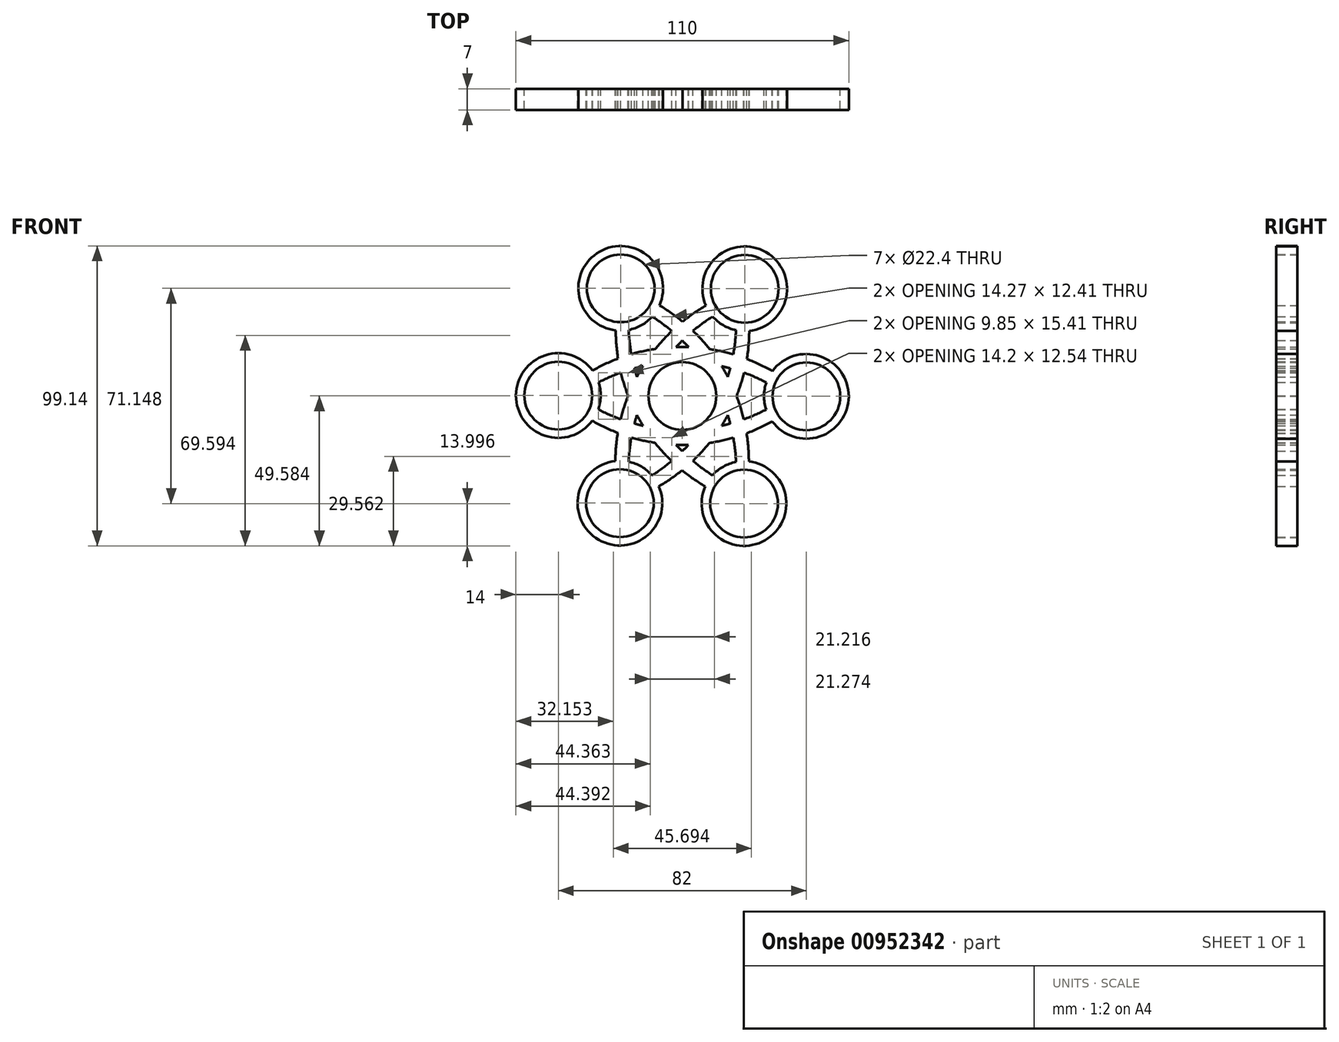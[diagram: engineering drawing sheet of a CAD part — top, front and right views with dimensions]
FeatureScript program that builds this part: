
annotation { "Feature Type Name" : "Feature", "Feature Type Description" : "" }
export const myFeature = defineFeature(function(context is Context, id is Id, definition is map)
    precondition{}
    {
        {
            var Q0;
            Q0=qCreatedBy(makeId("Front.planeOp"),FACE);
            var sketch = newSketch(context, id + "F0", { "sketchPlane" : qUnion([Q0])});
            skCircle(sketch, "E0", {"center": v(0, 0) * mm, "radius": 11.2 * mm});
            skCircle(sketch, "E1.cCircle", {"center": v(0, 0) * mm, "radius": 35.5 * mm, "construction": true});
            skLineSegment(sketch, "E1.0", {"start": v(20.62, 35.44) * mm, "end": v(41, -0.13) * mm});
            skLineSegment(sketch, "E1.1", {"start": v(41, -0.13) * mm, "end": v(20.38, -35.57) * mm});
            skLineSegment(sketch, "E1.2", {"start": v(20.38, -35.57) * mm, "end": v(-20.62, -35.44) * mm});
            skLineSegment(sketch, "E1.3", {"start": v(-20.62, -35.44) * mm, "end": v(-41, 0.13) * mm});
            skLineSegment(sketch, "E1.4", {"start": v(-41, 0.13) * mm, "end": v(-20.38, 35.57) * mm});
            skLineSegment(sketch, "E1.5", {"start": v(-20.38, 35.57) * mm, "end": v(20.62, 35.44) * mm});
            skPoint(sketch, "E1.0.midPoint", {"position": v(30.8, 17.65) * mm});
            skArc(sketch, "E2", {"start": v(-20.62, -35.44) * mm, "mid": v(14, -8.14) * mm, "end": v(20.62, 35.44) * mm});
            skArc(sketch, "E3", {"start": v(20.62, 35.44) * mm, "mid": v(-14, 8.14) * mm, "end": v(-20.62, -35.44) * mm});
            skArc(sketch, "E4", {"start": v(20.38, -35.57) * mm, "mid": v(14.05, 8.05) * mm, "end": v(-20.38, 35.57) * mm});
            skArc(sketch, "E5", {"start": v(-20.38, 35.57) * mm, "mid": v(-14.05, -8.05) * mm, "end": v(20.38, -35.57) * mm});
            skArc(sketch, "E6", {"start": v(41, -0.13) * mm, "mid": v(0.05, 16.2) * mm, "end": v(-41, 0.13) * mm});
            skArc(sketch, "E7", {"start": v(-41, 0.13) * mm, "mid": v(-0.05, -16.2) * mm, "end": v(41, -0.13) * mm});
            skCircle(sketch, "E8.cCircle", {"center": v(0, 0) * mm, "radius": 30.31 * mm, "construction": true});
            skLineSegment(sketch, "E8.0", {"start": v(17.5, -30.31) * mm, "end": v(-17.5, -30.31) * mm});
            skLineSegment(sketch, "E8.1", {"start": v(-17.5, -30.31) * mm, "end": v(-35, 0) * mm});
            skLineSegment(sketch, "E8.2", {"start": v(-35, 0) * mm, "end": v(-17.5, 30.31) * mm});
            skLineSegment(sketch, "E8.3", {"start": v(-17.5, 30.31) * mm, "end": v(17.5, 30.31) * mm});
            skLineSegment(sketch, "E8.4", {"start": v(17.5, 30.31) * mm, "end": v(35, 0) * mm});
            skLineSegment(sketch, "E8.5", {"start": v(35, 0) * mm, "end": v(17.5, -30.31) * mm});
            skPoint(sketch, "E8.0.midPoint", {"position": v(0, -30.31) * mm});
            skArc(sketch, "E9", {"start": v(-17.5, -30.31) * mm, "mid": v(9.76, -5.63) * mm, "end": v(17.5, 30.31) * mm});
            skArc(sketch, "E10", {"start": v(17.5, 30.31) * mm, "mid": v(-9.76, 5.63) * mm, "end": v(-17.5, -30.31) * mm});
            skArc(sketch, "E11", {"start": v(17.5, -30.31) * mm, "mid": v(9.76, 5.63) * mm, "end": v(-17.5, 30.31) * mm});
            skArc(sketch, "E12", {"start": v(-17.5, 30.31) * mm, "mid": v(-9.76, -5.63) * mm, "end": v(17.5, -30.31) * mm});
            skArc(sketch, "E13", {"start": v(35, 0) * mm, "mid": v(0, 11.27) * mm, "end": v(-35, 0) * mm});
            skArc(sketch, "E14", {"start": v(-35, 0) * mm, "mid": v(0, -11.27) * mm, "end": v(35, 0) * mm});
            skCircle(sketch, "E15", {"center": v(20.62, 35.44) * mm, "radius": 14 * mm});
            skCircle(sketch, "E16", {"center": v(-20.38, 35.57) * mm, "radius": 14 * mm});
            skCircle(sketch, "E17", {"center": v(-41, 0.13) * mm, "radius": 14 * mm});
            skCircle(sketch, "E18", {"center": v(-20.62, -35.44) * mm, "radius": 14 * mm});
            skCircle(sketch, "E19", {"center": v(20.38, -35.57) * mm, "radius": 14 * mm});
            skCircle(sketch, "E20", {"center": v(41, -0.13) * mm, "radius": 14 * mm});
            skCircle(sketch, "E21", {"center": v(20.62, 35.44) * mm, "radius": 11.2 * mm});
            skCircle(sketch, "E22", {"center": v(41, -0.13) * mm, "radius": 11.2 * mm});
            skCircle(sketch, "E23", {"center": v(20.38, -35.57) * mm, "radius": 11.2 * mm});
            skCircle(sketch, "E24", {"center": v(-20.62, -35.44) * mm, "radius": 11.2 * mm});
            skCircle(sketch, "E25", {"center": v(-41, 0.13) * mm, "radius": 11.2 * mm});
            skCircle(sketch, "E26", {"center": v(-20.38, 35.57) * mm, "radius": 11.2 * mm});
            skSolve(sketch);
        }
        {
            var Q0;
            {var subQ0=sQuery(id+"F0.wireOp",EDGE,"E16");var subQ1=sQuery(id+"F0.wireOp",EDGE,"E1.4");var subQ2=makeQuery(id+"F0.imprint","INTERSECT",VERTEX,{"derivedFrom":[subQ1,subQ0]});Q0=makeQuery(id+"F0.imprint","IMPRINT",FACE,{"disambiguationData":[TD([[makeQuery(id+"F0.imprint","IMPRINT",EDGE,{"disambiguationData":[TD([[subQ2,-1.0]])],"derivedFrom":subQ1}),1.0]])]});}
            var Q1;
            {var subQ0=sQuery(id+"F0.wireOp",EDGE,"E16");var subQ1=sQuery(id+"F0.wireOp",EDGE,"E1.5");var subQ2=makeQuery(id+"F0.imprint","INTERSECT",VERTEX,{"derivedFrom":[subQ1,subQ0]});Q1=makeQuery(id+"F0.imprint","IMPRINT",FACE,{"disambiguationData":[TD([[makeQuery(id+"F0.imprint","IMPRINT",EDGE,{"disambiguationData":[TD([[subQ2,1.0]])],"derivedFrom":subQ1}),-1.0]])]});}
            var Q2;
            {var subQ0=sQuery(id+"F0.wireOp",EDGE,"E16");var subQ5=sQuery(id+"F0.wireOp",EDGE,"E4");var subQ6=makeQuery(id+"F0.imprint","INTERSECT",VERTEX,{"derivedFrom":[subQ5,subQ0]});Q2=makeQuery(id+"F0.imprint","IMPRINT",FACE,{"disambiguationData":[TD([[makeQuery(id+"F0.imprint","IMPRINT",EDGE,{"disambiguationData":[TD([[subQ6,-1.0]])],"derivedFrom":subQ5}),1.0]])]});}
            var Q3;
            {var subQ0=sQuery(id+"F0.wireOp",EDGE,"E8.3");var subQ1=sQuery(id+"F0.wireOp",EDGE,"E4");var subQ2=makeQuery(id+"F0.imprint","INTERSECT",VERTEX,{"derivedFrom":[subQ1,subQ0]});Q3=makeQuery(id+"F0.imprint","IMPRINT",FACE,{"disambiguationData":[TD([[makeQuery(id+"F0.imprint","IMPRINT",EDGE,{"disambiguationData":[TD([[subQ2,-1.0]])],"derivedFrom":subQ1}),1.0]])]});}
            var Q4;
            {var subQ0=sQuery(id+"F0.wireOp",EDGE,"E16");var subQ1=sQuery(id+"F0.wireOp",EDGE,"E11");var subQ2=makeQuery(id+"F0.imprint","INTERSECT",VERTEX,{"derivedFrom":[subQ1,subQ0]});Q4=makeQuery(id+"F0.imprint","IMPRINT",FACE,{"disambiguationData":[TD([[makeQuery(id+"F0.imprint","IMPRINT",EDGE,{"disambiguationData":[TD([[subQ2,-1.0]])],"derivedFrom":subQ1}),1.0]])]});}
            var Q5;
            {var subQ1=sQuery(id+"F0.wireOp",EDGE,"E5");var subQ5=sQuery(id+"F0.wireOp",EDGE,"E8.2");var subQ6=makeQuery(id+"F0.imprint","INTERSECT",VERTEX,{"derivedFrom":[subQ1,subQ5]});Q5=makeQuery(id+"F0.imprint","IMPRINT",FACE,{"disambiguationData":[TD([[makeQuery(id+"F0.imprint","IMPRINT",EDGE,{"disambiguationData":[TD([[subQ6,-1.0]])],"derivedFrom":subQ1}),1.0]])]});}
            var Q6;
            {var subQ5=sQuery(id+"F0.wireOp",EDGE,"E16");var subQ6=sQuery(id+"F0.wireOp",EDGE,"E1.4");var subQ7=makeQuery(id+"F0.imprint","INTERSECT",VERTEX,{"derivedFrom":[subQ6,subQ5]});Q6=makeQuery(id+"F0.imprint","IMPRINT",FACE,{"disambiguationData":[TD([[makeQuery(id+"F0.imprint","IMPRINT",EDGE,{"disambiguationData":[TD([[subQ7,-1.0]])],"derivedFrom":subQ6}),-1.0]])]});}
            var Q7;
            {var subQ0=sQuery(id+"F0.wireOp",EDGE,"E8.2");var subQ1=sQuery(id+"F0.wireOp",EDGE,"E5");var subQ2=makeQuery(id+"F0.imprint","INTERSECT",VERTEX,{"derivedFrom":[subQ1,subQ0]});Q7=makeQuery(id+"F0.imprint","IMPRINT",FACE,{"disambiguationData":[TD([[makeQuery(id+"F0.imprint","IMPRINT",EDGE,{"disambiguationData":[TD([[subQ2,-1.0]])],"derivedFrom":subQ1}),-1.0]])]});}
            var Q8;
            {var subQ0=sQuery(id+"F0.wireOp",EDGE,"E26");var subQ1=sQuery(id+"F0.wireOp",EDGE,"E5");var subQ2=makeQuery(id+"F0.imprint","INTERSECT",VERTEX,{"derivedFrom":[subQ1,subQ0]});Q8=makeQuery(id+"F0.imprint","IMPRINT",FACE,{"disambiguationData":[TD([[makeQuery(id+"F0.imprint","IMPRINT",EDGE,{"disambiguationData":[TD([[subQ2,-1.0]])],"derivedFrom":subQ1}),1.0]])]});}
            var Q9;
            {var subQ0=sQuery(id+"F0.wireOp",EDGE,"E16");var subQ1=sQuery(id+"F0.wireOp",EDGE,"E4");var subQ2=makeQuery(id+"F0.imprint","INTERSECT",VERTEX,{"derivedFrom":[subQ1,subQ0]});Q9=makeQuery(id+"F0.imprint","IMPRINT",FACE,{"disambiguationData":[TD([[makeQuery(id+"F0.imprint","IMPRINT",EDGE,{"disambiguationData":[TD([[subQ2,-1.0]])],"derivedFrom":subQ1}),-1.0]])]});}
            var Q10;
            {var subQ0=sQuery(id+"F0.wireOp",EDGE,"E4");var subQ1=sQuery(id+"F0.wireOp",EDGE,"E3");var subQ2=makeQuery(id+"F0.imprint","INTERSECT",VERTEX,{"derivedFrom":[subQ1,subQ0]});Q10=makeQuery(id+"F0.imprint","IMPRINT",FACE,{"disambiguationData":[TD([[makeQuery(id+"F0.imprint","IMPRINT",EDGE,{"disambiguationData":[TD([[subQ2,-1.0]])],"derivedFrom":subQ1}),-1.0]])]});}
            var Q11;
            {var subQ0=sQuery(id+"F0.wireOp",EDGE,"E16");var subQ1=sQuery(id+"F0.wireOp",EDGE,"E5");var subQ2=makeQuery(id+"F0.imprint","INTERSECT",VERTEX,{"derivedFrom":[subQ1,subQ0]});Q11=makeQuery(id+"F0.imprint","IMPRINT",FACE,{"disambiguationData":[TD([[makeQuery(id+"F0.imprint","IMPRINT",EDGE,{"disambiguationData":[TD([[subQ2,-1.0]])],"derivedFrom":subQ1}),1.0]])]});}
            var Q12;
            {var subQ0=sQuery(id+"F0.wireOp",EDGE,"E6");var subQ1=sQuery(id+"F0.wireOp",EDGE,"E5");var subQ2=makeQuery(id+"F0.imprint","INTERSECT",VERTEX,{"derivedFrom":[subQ1,subQ0]});Q12=makeQuery(id+"F0.imprint","IMPRINT",FACE,{"disambiguationData":[TD([[makeQuery(id+"F0.imprint","IMPRINT",EDGE,{"disambiguationData":[TD([[subQ2,-1.0]])],"derivedFrom":subQ1}),1.0]])]});}
            var Q13;
            {var subQ0=sQuery(id+"F0.wireOp",EDGE,"E6");var subQ1=sQuery(id+"F0.wireOp",EDGE,"E3");var subQ2=makeQuery(id+"F0.imprint","INTERSECT",VERTEX,{"derivedFrom":[subQ1,subQ0]});Q13=makeQuery(id+"F0.imprint","IMPRINT",FACE,{"disambiguationData":[TD([[makeQuery(id+"F0.imprint","IMPRINT",EDGE,{"disambiguationData":[TD([[subQ2,-1.0]])],"derivedFrom":subQ1}),-1.0]])]});}
            var Q14;
            {var subQ0=sQuery(id+"F0.wireOp",EDGE,"E11");var subQ1=sQuery(id+"F0.wireOp",EDGE,"E3");var subQ2=makeQuery(id+"F0.imprint","INTERSECT",VERTEX,{"derivedFrom":[subQ1,subQ0]});Q14=makeQuery(id+"F0.imprint","IMPRINT",FACE,{"disambiguationData":[TD([[makeQuery(id+"F0.imprint","IMPRINT",EDGE,{"disambiguationData":[TD([[subQ2,-1.0]])],"derivedFrom":subQ1}),1.0]])]});}
            var Q15;
            {var subQ0=sQuery(id+"F0.wireOp",EDGE,"E4");var subQ1=sQuery(id+"F0.wireOp",EDGE,"E3");var subQ2=makeQuery(id+"F0.imprint","INTERSECT",VERTEX,{"derivedFrom":[subQ1,subQ0]});Q15=makeQuery(id+"F0.imprint","IMPRINT",FACE,{"disambiguationData":[TD([[makeQuery(id+"F0.imprint","IMPRINT",EDGE,{"disambiguationData":[TD([[subQ2,-1.0]])],"derivedFrom":subQ1}),1.0]])]});}
            var Q16;
            {var subQ0=sQuery(id+"F0.wireOp",EDGE,"E6");var subQ1=sQuery(id+"F0.wireOp",EDGE,"E3");var subQ2=makeQuery(id+"F0.imprint","INTERSECT",VERTEX,{"derivedFrom":[subQ1,subQ0]});Q16=makeQuery(id+"F0.imprint","IMPRINT",FACE,{"disambiguationData":[TD([[makeQuery(id+"F0.imprint","IMPRINT",EDGE,{"disambiguationData":[TD([[subQ2,-1.0]])],"derivedFrom":subQ1}),1.0]])]});}
            var Q17;
            {var subQ0=sQuery(id+"F0.wireOp",EDGE,"E11");var subQ1=sQuery(id+"F0.wireOp",EDGE,"E6");var subQ2=makeQuery(id+"F0.imprint","INTERSECT",VERTEX,{"derivedFrom":[subQ1,subQ0]});Q17=makeQuery(id+"F0.imprint","IMPRINT",FACE,{"disambiguationData":[TD([[makeQuery(id+"F0.imprint","IMPRINT",EDGE,{"disambiguationData":[TD([[subQ2,-1.0]])],"derivedFrom":subQ1}),1.0]])]});}
            var Q18;
            {var subQ0=sQuery(id+"F0.wireOp",EDGE,"E6");var subQ1=sQuery(id+"F0.wireOp",EDGE,"E4");var subQ2=makeQuery(id+"F0.imprint","INTERSECT",VERTEX,{"derivedFrom":[subQ1,subQ0]});Q18=makeQuery(id+"F0.imprint","IMPRINT",FACE,{"disambiguationData":[TD([[makeQuery(id+"F0.imprint","IMPRINT",EDGE,{"disambiguationData":[TD([[subQ2,-1.0]])],"derivedFrom":subQ1}),1.0]])]});}
            var Q19;
            {var subQ0=sQuery(id+"F0.wireOp",EDGE,"E13");var subQ1=sQuery(id+"F0.wireOp",EDGE,"E4");var subQ2=makeQuery(id+"F0.imprint","INTERSECT",VERTEX,{"derivedFrom":[subQ1,subQ0]});Q19=makeQuery(id+"F0.imprint","IMPRINT",FACE,{"disambiguationData":[TD([[makeQuery(id+"F0.imprint","IMPRINT",EDGE,{"disambiguationData":[TD([[subQ2,-1.0]])],"derivedFrom":subQ1}),1.0]])]});}
            var Q20;
            {var subQ0=sQuery(id+"F0.wireOp",EDGE,"E12");var subQ1=sQuery(id+"F0.wireOp",EDGE,"E3");var subQ2=makeQuery(id+"F0.imprint","INTERSECT",VERTEX,{"derivedFrom":[subQ1,subQ0]});Q20=makeQuery(id+"F0.imprint","IMPRINT",FACE,{"disambiguationData":[TD([[makeQuery(id+"F0.imprint","IMPRINT",EDGE,{"disambiguationData":[TD([[subQ2,-1.0]])],"derivedFrom":subQ1}),-1.0]])]});}
            var Q21;
            {var subQ0=sQuery(id+"F0.wireOp",EDGE,"E12");var subQ1=sQuery(id+"F0.wireOp",EDGE,"E3");var subQ2=makeQuery(id+"F0.imprint","INTERSECT",VERTEX,{"derivedFrom":[subQ1,subQ0]});Q21=makeQuery(id+"F0.imprint","IMPRINT",FACE,{"disambiguationData":[TD([[makeQuery(id+"F0.imprint","IMPRINT",EDGE,{"disambiguationData":[TD([[subQ2,-1.0]])],"derivedFrom":subQ1}),1.0]])]});}
            var Q22;
            {var subQ0=sQuery(id+"F0.wireOp",EDGE,"E13");var subQ1=sQuery(id+"F0.wireOp",EDGE,"E3");var subQ2=makeQuery(id+"F0.imprint","INTERSECT",VERTEX,{"derivedFrom":[subQ1,subQ0]});Q22=makeQuery(id+"F0.imprint","IMPRINT",FACE,{"disambiguationData":[TD([[makeQuery(id+"F0.imprint","IMPRINT",EDGE,{"disambiguationData":[TD([[subQ2,-1.0]])],"derivedFrom":subQ1}),1.0]])]});}
            var Q23;
            Q23=makeQuery(id+"F0.imprint","IMPRINT",FACE,{"disambiguationData":[TD([[makeQuery(id+"F0.imprint","IMPRINT",EDGE,{"derivedFrom":sQuery(id+"F0.wireOp",EDGE,"E0")}),-1.0]])]});
            var Q24;
            {var subQ0=sQuery(id+"F0.wireOp",EDGE,"E9");var subQ1=sQuery(id+"F0.wireOp",EDGE,"E4");var subQ2=makeQuery(id+"F0.imprint","INTERSECT",VERTEX,{"derivedFrom":[subQ1,subQ0]});Q24=makeQuery(id+"F0.imprint","IMPRINT",FACE,{"disambiguationData":[TD([[makeQuery(id+"F0.imprint","IMPRINT",EDGE,{"disambiguationData":[TD([[subQ2,-1.0]])],"derivedFrom":subQ1}),1.0]])]});}
            var Q25;
            {var subQ0=sQuery(id+"F0.wireOp",EDGE,"E11");var subQ1=sQuery(id+"F0.wireOp",EDGE,"E2");var subQ2=makeQuery(id+"F0.imprint","INTERSECT",VERTEX,{"derivedFrom":[subQ1,subQ0]});Q25=makeQuery(id+"F0.imprint","IMPRINT",FACE,{"disambiguationData":[TD([[makeQuery(id+"F0.imprint","IMPRINT",EDGE,{"disambiguationData":[TD([[subQ2,-1.0]])],"derivedFrom":subQ1}),1.0]])]});}
            var Q26;
            {var subQ0=sQuery(id+"F0.wireOp",EDGE,"E14");var subQ1=sQuery(id+"F0.wireOp",EDGE,"E2");var subQ2=makeQuery(id+"F0.imprint","INTERSECT",VERTEX,{"derivedFrom":[subQ1,subQ0]});Q26=makeQuery(id+"F0.imprint","IMPRINT",FACE,{"disambiguationData":[TD([[makeQuery(id+"F0.imprint","IMPRINT",EDGE,{"disambiguationData":[TD([[subQ2,-1.0]])],"derivedFrom":subQ1}),1.0]])]});}
            var Q27;
            {var subQ0=sQuery(id+"F0.wireOp",EDGE,"E7");var subQ1=sQuery(id+"F0.wireOp",EDGE,"E2");var subQ2=makeQuery(id+"F0.imprint","INTERSECT",VERTEX,{"derivedFrom":[subQ1,subQ0]});Q27=makeQuery(id+"F0.imprint","IMPRINT",FACE,{"disambiguationData":[TD([[makeQuery(id+"F0.imprint","IMPRINT",EDGE,{"disambiguationData":[TD([[subQ2,-1.0]])],"derivedFrom":subQ1}),1.0]])]});}
            var Q28;
            {var subQ0=sQuery(id+"F0.wireOp",EDGE,"E10");var subQ1=sQuery(id+"F0.wireOp",EDGE,"E5");var subQ2=makeQuery(id+"F0.imprint","INTERSECT",VERTEX,{"derivedFrom":[subQ1,subQ0]});Q28=makeQuery(id+"F0.imprint","IMPRINT",FACE,{"disambiguationData":[TD([[makeQuery(id+"F0.imprint","IMPRINT",EDGE,{"disambiguationData":[TD([[subQ2,-1.0]])],"derivedFrom":subQ1}),1.0]])]});}
            var Q29;
            {var subQ0=sQuery(id+"F0.wireOp",EDGE,"E12");var subQ1=sQuery(id+"F0.wireOp",EDGE,"E7");var subQ2=makeQuery(id+"F0.imprint","INTERSECT",VERTEX,{"derivedFrom":[subQ1,subQ0]});Q29=makeQuery(id+"F0.imprint","IMPRINT",FACE,{"disambiguationData":[TD([[makeQuery(id+"F0.imprint","IMPRINT",EDGE,{"disambiguationData":[TD([[subQ2,-1.0]])],"derivedFrom":subQ1}),1.0]])]});}
            var Q30;
            {var subQ0=sQuery(id+"F0.wireOp",EDGE,"E14");var subQ1=sQuery(id+"F0.wireOp",EDGE,"E5");var subQ2=makeQuery(id+"F0.imprint","INTERSECT",VERTEX,{"derivedFrom":[subQ1,subQ0]});Q30=makeQuery(id+"F0.imprint","IMPRINT",FACE,{"disambiguationData":[TD([[makeQuery(id+"F0.imprint","IMPRINT",EDGE,{"disambiguationData":[TD([[subQ2,-1.0]])],"derivedFrom":subQ1}),1.0]])]});}
            var Q31;
            {var subQ0=sQuery(id+"F0.wireOp",EDGE,"E14");var subQ1=sQuery(id+"F0.wireOp",EDGE,"E5");var subQ2=makeQuery(id+"F0.imprint","INTERSECT",VERTEX,{"derivedFrom":[subQ1,subQ0]});Q31=makeQuery(id+"F0.imprint","IMPRINT",FACE,{"disambiguationData":[TD([[makeQuery(id+"F0.imprint","IMPRINT",EDGE,{"disambiguationData":[TD([[subQ2,-1.0]])],"derivedFrom":subQ1}),-1.0]])]});}
            var Q32;
            {var subQ0=sQuery(id+"F0.wireOp",EDGE,"E15");var subQ1=sQuery(id+"F0.wireOp",EDGE,"E1.0");var subQ2=makeQuery(id+"F0.imprint","INTERSECT",VERTEX,{"derivedFrom":[subQ1,subQ0]});Q32=makeQuery(id+"F0.imprint","IMPRINT",FACE,{"disambiguationData":[TD([[makeQuery(id+"F0.imprint","IMPRINT",EDGE,{"disambiguationData":[TD([[subQ2,1.0]])],"derivedFrom":subQ1}),1.0]])]});}
            var Q33;
            {var subQ0=sQuery(id+"F0.wireOp",EDGE,"E20");var subQ1=sQuery(id+"F0.wireOp",EDGE,"E1.0");var subQ2=makeQuery(id+"F0.imprint","INTERSECT",VERTEX,{"derivedFrom":[subQ1,subQ0]});Q33=makeQuery(id+"F0.imprint","IMPRINT",FACE,{"disambiguationData":[TD([[makeQuery(id+"F0.imprint","IMPRINT",EDGE,{"disambiguationData":[TD([[subQ2,-1.0]])],"derivedFrom":subQ1}),1.0]])]});}
            var Q34;
            {var subQ0=sQuery(id+"F0.wireOp",EDGE,"E19");var subQ1=sQuery(id+"F0.wireOp",EDGE,"E1.1");var subQ2=makeQuery(id+"F0.imprint","INTERSECT",VERTEX,{"derivedFrom":[subQ1,subQ0]});Q34=makeQuery(id+"F0.imprint","IMPRINT",FACE,{"disambiguationData":[TD([[makeQuery(id+"F0.imprint","IMPRINT",EDGE,{"disambiguationData":[TD([[subQ2,-1.0]])],"derivedFrom":subQ1}),1.0]])]});}
            var Q35;
            {var subQ0=sQuery(id+"F0.wireOp",EDGE,"E18");var subQ1=sQuery(id+"F0.wireOp",EDGE,"E1.2");var subQ2=makeQuery(id+"F0.imprint","INTERSECT",VERTEX,{"derivedFrom":[subQ1,subQ0]});Q35=makeQuery(id+"F0.imprint","IMPRINT",FACE,{"disambiguationData":[TD([[makeQuery(id+"F0.imprint","IMPRINT",EDGE,{"disambiguationData":[TD([[subQ2,-1.0]])],"derivedFrom":subQ1}),1.0]])]});}
            var Q36;
            {var subQ0=sQuery(id+"F0.wireOp",EDGE,"E17");var subQ1=sQuery(id+"F0.wireOp",EDGE,"E1.3");var subQ2=makeQuery(id+"F0.imprint","INTERSECT",VERTEX,{"derivedFrom":[subQ1,subQ0]});Q36=makeQuery(id+"F0.imprint","IMPRINT",FACE,{"disambiguationData":[TD([[makeQuery(id+"F0.imprint","IMPRINT",EDGE,{"disambiguationData":[TD([[subQ2,-1.0]])],"derivedFrom":subQ1}),1.0]])]});}
            var Q37;
            {var subQ3=sQuery(id+"F0.wireOp",EDGE,"E15");var subQ7=sQuery(id+"F0.wireOp",EDGE,"E1.0");var subQ8=makeQuery(id+"F0.imprint","INTERSECT",VERTEX,{"derivedFrom":[subQ7,subQ3]});Q37=makeQuery(id+"F0.imprint","IMPRINT",FACE,{"disambiguationData":[TD([[makeQuery(id+"F0.imprint","IMPRINT",EDGE,{"disambiguationData":[TD([[subQ8,1.0]])],"derivedFrom":subQ7}),-1.0]])]});}
            var Q38;
            {var subQ0=sQuery(id+"F0.wireOp",EDGE,"E8.4");var subQ1=sQuery(id+"F0.wireOp",EDGE,"E2");var subQ2=makeQuery(id+"F0.imprint","INTERSECT",VERTEX,{"derivedFrom":[subQ1,subQ0]});Q38=makeQuery(id+"F0.imprint","IMPRINT",FACE,{"disambiguationData":[TD([[makeQuery(id+"F0.imprint","IMPRINT",EDGE,{"disambiguationData":[TD([[subQ2,-1.0]])],"derivedFrom":subQ1}),1.0]])]});}
            var Q39;
            {var subQ0=sQuery(id+"F0.wireOp",EDGE,"E15");var subQ1=sQuery(id+"F0.wireOp",EDGE,"E2");var subQ2=makeQuery(id+"F0.imprint","INTERSECT",VERTEX,{"derivedFrom":[subQ1,subQ0]});Q39=makeQuery(id+"F0.imprint","IMPRINT",FACE,{"disambiguationData":[TD([[makeQuery(id+"F0.imprint","IMPRINT",EDGE,{"disambiguationData":[TD([[subQ2,-1.0]])],"derivedFrom":subQ1}),-1.0]])]});}
            var Q40;
            {var subQ0=sQuery(id+"F0.wireOp",EDGE,"E15");var subQ5=sQuery(id+"F0.wireOp",EDGE,"E2");var subQ6=makeQuery(id+"F0.imprint","INTERSECT",VERTEX,{"derivedFrom":[subQ5,subQ0]});Q40=makeQuery(id+"F0.imprint","IMPRINT",FACE,{"disambiguationData":[TD([[makeQuery(id+"F0.imprint","IMPRINT",EDGE,{"disambiguationData":[TD([[subQ6,-1.0]])],"derivedFrom":subQ5}),1.0]])]});}
            var Q41;
            {var subQ0=sQuery(id+"F0.wireOp",EDGE,"E15");var subQ1=sQuery(id+"F0.wireOp",EDGE,"E9");var subQ2=makeQuery(id+"F0.imprint","INTERSECT",VERTEX,{"derivedFrom":[subQ1,subQ0]});Q41=makeQuery(id+"F0.imprint","IMPRINT",FACE,{"disambiguationData":[TD([[makeQuery(id+"F0.imprint","IMPRINT",EDGE,{"disambiguationData":[TD([[subQ2,-1.0]])],"derivedFrom":subQ1}),1.0]])]});}
            var Q42;
            {var subQ5=sQuery(id+"F0.wireOp",EDGE,"E3");var subQ7=sQuery(id+"F0.wireOp",EDGE,"E8.3");var subQ8=makeQuery(id+"F0.imprint","INTERSECT",VERTEX,{"derivedFrom":[subQ5,subQ7]});Q42=makeQuery(id+"F0.imprint","IMPRINT",FACE,{"disambiguationData":[TD([[makeQuery(id+"F0.imprint","IMPRINT",EDGE,{"disambiguationData":[TD([[subQ8,-1.0]])],"derivedFrom":subQ5}),1.0]])]});}
            var Q43;
            {var subQ0=sQuery(id+"F0.wireOp",EDGE,"E15");var subQ1=sQuery(id+"F0.wireOp",EDGE,"E1.5");var subQ2=makeQuery(id+"F0.imprint","INTERSECT",VERTEX,{"derivedFrom":[subQ1,subQ0]});Q43=makeQuery(id+"F0.imprint","IMPRINT",FACE,{"disambiguationData":[TD([[makeQuery(id+"F0.imprint","IMPRINT",EDGE,{"disambiguationData":[TD([[subQ2,-1.0]])],"derivedFrom":subQ1}),-1.0]])]});}
            var Q44;
            {var subQ0=sQuery(id+"F0.wireOp",EDGE,"E21");var subQ1=sQuery(id+"F0.wireOp",EDGE,"E3");var subQ2=makeQuery(id+"F0.imprint","INTERSECT",VERTEX,{"derivedFrom":[subQ1,subQ0]});Q44=makeQuery(id+"F0.imprint","IMPRINT",FACE,{"disambiguationData":[TD([[makeQuery(id+"F0.imprint","IMPRINT",EDGE,{"disambiguationData":[TD([[subQ2,-1.0]])],"derivedFrom":subQ1}),1.0]])]});}
            var Q45;
            {var subQ0=sQuery(id+"F0.wireOp",EDGE,"E8.3");var subQ1=sQuery(id+"F0.wireOp",EDGE,"E3");var subQ2=makeQuery(id+"F0.imprint","INTERSECT",VERTEX,{"derivedFrom":[subQ1,subQ0]});Q45=makeQuery(id+"F0.imprint","IMPRINT",FACE,{"disambiguationData":[TD([[makeQuery(id+"F0.imprint","IMPRINT",EDGE,{"disambiguationData":[TD([[subQ2,-1.0]])],"derivedFrom":subQ1}),-1.0]])]});}
            var Q46;
            {var subQ0=sQuery(id+"F0.wireOp",EDGE,"E15");var subQ1=sQuery(id+"F0.wireOp",EDGE,"E3");var subQ2=makeQuery(id+"F0.imprint","INTERSECT",VERTEX,{"derivedFrom":[subQ1,subQ0]});Q46=makeQuery(id+"F0.imprint","IMPRINT",FACE,{"disambiguationData":[TD([[makeQuery(id+"F0.imprint","IMPRINT",EDGE,{"disambiguationData":[TD([[subQ2,-1.0]])],"derivedFrom":subQ1}),1.0]])]});}
            var Q47;
            {var subQ0=sQuery(id+"F0.wireOp",EDGE,"E6");var subQ1=sQuery(id+"F0.wireOp",EDGE,"E2");var subQ2=makeQuery(id+"F0.imprint","INTERSECT",VERTEX,{"derivedFrom":[subQ1,subQ0]});Q47=makeQuery(id+"F0.imprint","IMPRINT",FACE,{"disambiguationData":[TD([[makeQuery(id+"F0.imprint","IMPRINT",EDGE,{"disambiguationData":[TD([[subQ2,-1.0]])],"derivedFrom":subQ1}),1.0]])]});}
            var Q48;
            {var subQ0=sQuery(id+"F0.wireOp",EDGE,"E13");var subQ1=sQuery(id+"F0.wireOp",EDGE,"E2");var subQ2=makeQuery(id+"F0.imprint","INTERSECT",VERTEX,{"derivedFrom":[subQ1,subQ0]});Q48=makeQuery(id+"F0.imprint","IMPRINT",FACE,{"disambiguationData":[TD([[makeQuery(id+"F0.imprint","IMPRINT",EDGE,{"disambiguationData":[TD([[subQ2,-1.0]])],"derivedFrom":subQ1}),1.0]])]});}
            var Q49;
            {var subQ0=sQuery(id+"F0.wireOp",EDGE,"E5");var subQ1=sQuery(id+"F0.wireOp",EDGE,"E3");var subQ2=makeQuery(id+"F0.imprint","INTERSECT",VERTEX,{"derivedFrom":[subQ1,subQ0]});Q49=makeQuery(id+"F0.imprint","IMPRINT",FACE,{"disambiguationData":[TD([[makeQuery(id+"F0.imprint","IMPRINT",EDGE,{"disambiguationData":[TD([[subQ2,-1.0]])],"derivedFrom":subQ1}),1.0]])]});}
            var Q50;
            {var subQ0=sQuery(id+"F0.wireOp",EDGE,"E14");var subQ1=sQuery(id+"F0.wireOp",EDGE,"E3");var subQ2=makeQuery(id+"F0.imprint","INTERSECT",VERTEX,{"derivedFrom":[subQ1,subQ0]});Q50=makeQuery(id+"F0.imprint","IMPRINT",FACE,{"disambiguationData":[TD([[makeQuery(id+"F0.imprint","IMPRINT",EDGE,{"disambiguationData":[TD([[subQ2,-1.0]])],"derivedFrom":subQ1}),1.0]])]});}
            var Q51;
            {var subQ0=sQuery(id+"F0.wireOp",EDGE,"E4");var subQ1=sQuery(id+"F0.wireOp",EDGE,"E2");var subQ2=makeQuery(id+"F0.imprint","INTERSECT",VERTEX,{"derivedFrom":[subQ1,subQ0]});Q51=makeQuery(id+"F0.imprint","IMPRINT",FACE,{"disambiguationData":[TD([[makeQuery(id+"F0.imprint","IMPRINT",EDGE,{"disambiguationData":[TD([[subQ2,-1.0]])],"derivedFrom":subQ1}),1.0]])]});}
            var Q52;
            {var subQ0=sQuery(id+"F0.wireOp",EDGE,"E13");var subQ1=sQuery(id+"F0.wireOp",EDGE,"E4");var subQ2=makeQuery(id+"F0.imprint","INTERSECT",VERTEX,{"derivedFrom":[subQ1,subQ0]});Q52=makeQuery(id+"F0.imprint","IMPRINT",FACE,{"disambiguationData":[TD([[makeQuery(id+"F0.imprint","IMPRINT",EDGE,{"disambiguationData":[TD([[subQ2,-1.0]])],"derivedFrom":subQ1}),-1.0]])]});}
            var Q53;
            {var subQ0=sQuery(id+"F0.wireOp",EDGE,"E7");var subQ1=sQuery(id+"F0.wireOp",EDGE,"E2");var subQ2=makeQuery(id+"F0.imprint","INTERSECT",VERTEX,{"derivedFrom":[subQ1,subQ0]});Q53=makeQuery(id+"F0.imprint","IMPRINT",FACE,{"disambiguationData":[TD([[makeQuery(id+"F0.imprint","IMPRINT",EDGE,{"disambiguationData":[TD([[subQ2,-1.0]])],"derivedFrom":subQ1}),-1.0]])]});}
            var Q54;
            {var subQ0=sQuery(id+"F0.wireOp",EDGE,"E11");var subQ1=sQuery(id+"F0.wireOp",EDGE,"E2");var subQ2=makeQuery(id+"F0.imprint","INTERSECT",VERTEX,{"derivedFrom":[subQ1,subQ0]});Q54=makeQuery(id+"F0.imprint","IMPRINT",FACE,{"disambiguationData":[TD([[makeQuery(id+"F0.imprint","IMPRINT",EDGE,{"disambiguationData":[TD([[subQ2,-1.0]])],"derivedFrom":subQ1}),-1.0]])]});}
            var Q55;
            {var subQ0=sQuery(id+"F0.wireOp",EDGE,"E7");var subQ1=sQuery(id+"F0.wireOp",EDGE,"E4");var subQ2=makeQuery(id+"F0.imprint","INTERSECT",VERTEX,{"derivedFrom":[subQ1,subQ0]});Q55=makeQuery(id+"F0.imprint","IMPRINT",FACE,{"disambiguationData":[TD([[makeQuery(id+"F0.imprint","IMPRINT",EDGE,{"disambiguationData":[TD([[subQ2,-1.0]])],"derivedFrom":subQ1}),1.0]])]});}
            var Q56;
            {var subQ0=sQuery(id+"F0.wireOp",EDGE,"E7");var subQ1=sQuery(id+"F0.wireOp",EDGE,"E5");var subQ2=makeQuery(id+"F0.imprint","INTERSECT",VERTEX,{"derivedFrom":[subQ1,subQ0]});Q56=makeQuery(id+"F0.imprint","IMPRINT",FACE,{"disambiguationData":[TD([[makeQuery(id+"F0.imprint","IMPRINT",EDGE,{"disambiguationData":[TD([[subQ2,-1.0]])],"derivedFrom":subQ1}),1.0]])]});}
            var Q57;
            {var subQ0=sQuery(id+"F0.wireOp",EDGE,"E12");var subQ1=sQuery(id+"F0.wireOp",EDGE,"E2");var subQ2=makeQuery(id+"F0.imprint","INTERSECT",VERTEX,{"derivedFrom":[subQ1,subQ0]});Q57=makeQuery(id+"F0.imprint","IMPRINT",FACE,{"disambiguationData":[TD([[makeQuery(id+"F0.imprint","IMPRINT",EDGE,{"disambiguationData":[TD([[subQ2,-1.0]])],"derivedFrom":subQ1}),1.0]])]});}
            var Q58;
            {var subQ0=sQuery(id+"F0.wireOp",EDGE,"E5");var subQ1=sQuery(id+"F0.wireOp",EDGE,"E2");var subQ2=makeQuery(id+"F0.imprint","INTERSECT",VERTEX,{"derivedFrom":[subQ1,subQ0]});Q58=makeQuery(id+"F0.imprint","IMPRINT",FACE,{"disambiguationData":[TD([[makeQuery(id+"F0.imprint","IMPRINT",EDGE,{"disambiguationData":[TD([[subQ2,-1.0]])],"derivedFrom":subQ1}),1.0]])]});}
            var Q59;
            {var subQ0=sQuery(id+"F0.wireOp",EDGE,"E5");var subQ1=sQuery(id+"F0.wireOp",EDGE,"E2");var subQ2=makeQuery(id+"F0.imprint","INTERSECT",VERTEX,{"derivedFrom":[subQ1,subQ0]});Q59=makeQuery(id+"F0.imprint","IMPRINT",FACE,{"disambiguationData":[TD([[makeQuery(id+"F0.imprint","IMPRINT",EDGE,{"disambiguationData":[TD([[subQ2,-1.0]])],"derivedFrom":subQ1}),-1.0]])]});}
            var Q60;
            {var subQ0=sQuery(id+"F0.wireOp",EDGE,"E19");var subQ1=sQuery(id+"F0.wireOp",EDGE,"E4");var subQ2=makeQuery(id+"F0.imprint","INTERSECT",VERTEX,{"derivedFrom":[subQ1,subQ0]});Q60=makeQuery(id+"F0.imprint","IMPRINT",FACE,{"disambiguationData":[TD([[makeQuery(id+"F0.imprint","IMPRINT",EDGE,{"disambiguationData":[TD([[subQ2,-1.0]])],"derivedFrom":subQ1}),1.0]])]});}
            var Q61;
            {var subQ0=sQuery(id+"F0.wireOp",EDGE,"E7");var subQ1=sQuery(id+"F0.wireOp",EDGE,"E3");var subQ2=makeQuery(id+"F0.imprint","INTERSECT",VERTEX,{"derivedFrom":[subQ1,subQ0]});Q61=makeQuery(id+"F0.imprint","IMPRINT",FACE,{"disambiguationData":[TD([[makeQuery(id+"F0.imprint","IMPRINT",EDGE,{"disambiguationData":[TD([[subQ2,-1.0]])],"derivedFrom":subQ1}),1.0]])]});}
            var Q62;
            {var subQ0=sQuery(id+"F0.wireOp",EDGE,"E18");var subQ1=sQuery(id+"F0.wireOp",EDGE,"E2");var subQ2=makeQuery(id+"F0.imprint","INTERSECT",VERTEX,{"derivedFrom":[subQ1,subQ0]});Q62=makeQuery(id+"F0.imprint","IMPRINT",FACE,{"disambiguationData":[TD([[makeQuery(id+"F0.imprint","IMPRINT",EDGE,{"disambiguationData":[TD([[subQ2,-1.0]])],"derivedFrom":subQ1}),1.0]])]});}
            var Q63;
            {var subQ0=sQuery(id+"F0.wireOp",EDGE,"E7");var subQ1=sQuery(id+"F0.wireOp",EDGE,"E4");var subQ2=makeQuery(id+"F0.imprint","INTERSECT",VERTEX,{"derivedFrom":[subQ1,subQ0]});Q63=makeQuery(id+"F0.imprint","IMPRINT",FACE,{"disambiguationData":[TD([[makeQuery(id+"F0.imprint","IMPRINT",EDGE,{"disambiguationData":[TD([[subQ2,-1.0]])],"derivedFrom":subQ1}),-1.0]])]});}
            var Q64;
            {var subQ0=sQuery(id+"F0.wireOp",EDGE,"E13");var subQ1=sQuery(id+"F0.wireOp",EDGE,"E2");var subQ2=makeQuery(id+"F0.imprint","INTERSECT",VERTEX,{"derivedFrom":[subQ1,subQ0]});Q64=makeQuery(id+"F0.imprint","IMPRINT",FACE,{"disambiguationData":[TD([[makeQuery(id+"F0.imprint","IMPRINT",EDGE,{"disambiguationData":[TD([[subQ2,-1.0]])],"derivedFrom":subQ1}),-1.0]])]});}
            var Q65;
            {var subQ0=sQuery(id+"F0.wireOp",EDGE,"E20");var subQ1=sQuery(id+"F0.wireOp",EDGE,"E1.0");var subQ2=makeQuery(id+"F0.imprint","INTERSECT",VERTEX,{"derivedFrom":[subQ1,subQ0]});Q65=makeQuery(id+"F0.imprint","IMPRINT",FACE,{"disambiguationData":[TD([[makeQuery(id+"F0.imprint","IMPRINT",EDGE,{"disambiguationData":[TD([[subQ2,-1.0]])],"derivedFrom":subQ1}),-1.0]])]});}
            var Q66;
            {var subQ0=sQuery(id+"F0.wireOp",EDGE,"E22");var subQ1=sQuery(id+"F0.wireOp",EDGE,"E6");var subQ2=makeQuery(id+"F0.imprint","INTERSECT",VERTEX,{"derivedFrom":[subQ1,subQ0]});Q66=makeQuery(id+"F0.imprint","IMPRINT",FACE,{"disambiguationData":[TD([[makeQuery(id+"F0.imprint","IMPRINT",EDGE,{"disambiguationData":[TD([[subQ2,-1.0]])],"derivedFrom":subQ1}),1.0]])]});}
            var Q67;
            {var subQ0=sQuery(id+"F0.wireOp",EDGE,"E8.4");var subQ1=sQuery(id+"F0.wireOp",EDGE,"E6");var subQ2=makeQuery(id+"F0.imprint","INTERSECT",VERTEX,{"derivedFrom":[subQ1,subQ0]});Q67=makeQuery(id+"F0.imprint","IMPRINT",FACE,{"disambiguationData":[TD([[makeQuery(id+"F0.imprint","IMPRINT",EDGE,{"disambiguationData":[TD([[subQ2,-1.0]])],"derivedFrom":subQ1}),-1.0]])]});}
            var Q68;
            {var subQ5=sQuery(id+"F0.wireOp",EDGE,"E8.4");var subQ6=sQuery(id+"F0.wireOp",EDGE,"E6");var subQ7=makeQuery(id+"F0.imprint","INTERSECT",VERTEX,{"derivedFrom":[subQ6,subQ5]});Q68=makeQuery(id+"F0.imprint","IMPRINT",FACE,{"disambiguationData":[TD([[makeQuery(id+"F0.imprint","IMPRINT",EDGE,{"disambiguationData":[TD([[subQ7,-1.0]])],"derivedFrom":subQ6}),1.0]])]});}
            var Q69;
            {var subQ0=sQuery(id+"F0.wireOp",EDGE,"E22");var subQ1=sQuery(id+"F0.wireOp",EDGE,"E13");var subQ2=makeQuery(id+"F0.imprint","INTERSECT",VERTEX,{"derivedFrom":[subQ1,subQ0]});Q69=makeQuery(id+"F0.imprint","IMPRINT",FACE,{"disambiguationData":[TD([[makeQuery(id+"F0.imprint","IMPRINT",EDGE,{"disambiguationData":[TD([[subQ2,-1.0]])],"derivedFrom":subQ1}),1.0]])]});}
            var Q70;
            {var subQ0=sQuery(id+"F0.wireOp",EDGE,"E20");var subQ1=sQuery(id+"F0.wireOp",EDGE,"E7");var subQ2=makeQuery(id+"F0.imprint","INTERSECT",VERTEX,{"derivedFrom":[subQ1,subQ0]});Q70=makeQuery(id+"F0.imprint","IMPRINT",FACE,{"disambiguationData":[TD([[makeQuery(id+"F0.imprint","IMPRINT",EDGE,{"disambiguationData":[TD([[subQ2,-1.0]])],"derivedFrom":subQ1}),1.0]])]});}
            var Q71;
            {var subQ0=sQuery(id+"F0.wireOp",EDGE,"E8.5");var subQ1=sQuery(id+"F0.wireOp",EDGE,"E7");var subQ2=makeQuery(id+"F0.imprint","INTERSECT",VERTEX,{"derivedFrom":[subQ1,subQ0]});Q71=makeQuery(id+"F0.imprint","IMPRINT",FACE,{"disambiguationData":[TD([[makeQuery(id+"F0.imprint","IMPRINT",EDGE,{"disambiguationData":[TD([[subQ2,-1.0]])],"derivedFrom":subQ1}),1.0]])]});}
            var Q72;
            {var subQ3=sQuery(id+"F0.wireOp",EDGE,"E20");var subQ7=sQuery(id+"F0.wireOp",EDGE,"E1.1");var subQ8=makeQuery(id+"F0.imprint","INTERSECT",VERTEX,{"derivedFrom":[subQ7,subQ3]});Q72=makeQuery(id+"F0.imprint","IMPRINT",FACE,{"disambiguationData":[TD([[makeQuery(id+"F0.imprint","IMPRINT",EDGE,{"disambiguationData":[TD([[subQ8,1.0]])],"derivedFrom":subQ7}),-1.0]])]});}
            var Q73;
            {var subQ0=sQuery(id+"F0.wireOp",EDGE,"E20");var subQ1=sQuery(id+"F0.wireOp",EDGE,"E7");var subQ2=makeQuery(id+"F0.imprint","INTERSECT",VERTEX,{"derivedFrom":[subQ1,subQ0]});Q73=makeQuery(id+"F0.imprint","IMPRINT",FACE,{"disambiguationData":[TD([[makeQuery(id+"F0.imprint","IMPRINT",EDGE,{"disambiguationData":[TD([[subQ2,-1.0]])],"derivedFrom":subQ1}),-1.0]])]});}
            var Q74;
            {var subQ0=sQuery(id+"F0.wireOp",EDGE,"E6");var subQ1=sQuery(id+"F0.wireOp",EDGE,"E5");var subQ2=makeQuery(id+"F0.imprint","INTERSECT",VERTEX,{"derivedFrom":[subQ1,subQ0]});Q74=makeQuery(id+"F0.imprint","IMPRINT",FACE,{"disambiguationData":[TD([[makeQuery(id+"F0.imprint","IMPRINT",EDGE,{"disambiguationData":[TD([[subQ2,-1.0]])],"derivedFrom":subQ1}),-1.0]])]});}
            var Q75;
            {var subQ0=sQuery(id+"F0.wireOp",EDGE,"E14");var subQ1=sQuery(id+"F0.wireOp",EDGE,"E3");var subQ2=makeQuery(id+"F0.imprint","INTERSECT",VERTEX,{"derivedFrom":[subQ1,subQ0]});Q75=makeQuery(id+"F0.imprint","IMPRINT",FACE,{"disambiguationData":[TD([[makeQuery(id+"F0.imprint","IMPRINT",EDGE,{"disambiguationData":[TD([[subQ2,-1.0]])],"derivedFrom":subQ1}),-1.0]])]});}
            var Q76;
            {var subQ0=sQuery(id+"F0.wireOp",EDGE,"E17");var subQ1=sQuery(id+"F0.wireOp",EDGE,"E13");var subQ2=makeQuery(id+"F0.imprint","INTERSECT",VERTEX,{"derivedFrom":[subQ1,subQ0]});Q76=makeQuery(id+"F0.imprint","IMPRINT",FACE,{"disambiguationData":[TD([[makeQuery(id+"F0.imprint","IMPRINT",EDGE,{"disambiguationData":[TD([[subQ2,-1.0]])],"derivedFrom":subQ1}),1.0]])]});}
            var Q77;
            {var subQ0=sQuery(id+"F0.wireOp",EDGE,"E17");var subQ1=sQuery(id+"F0.wireOp",EDGE,"E6");var subQ2=makeQuery(id+"F0.imprint","INTERSECT",VERTEX,{"derivedFrom":[subQ1,subQ0]});Q77=makeQuery(id+"F0.imprint","IMPRINT",FACE,{"disambiguationData":[TD([[makeQuery(id+"F0.imprint","IMPRINT",EDGE,{"disambiguationData":[TD([[subQ2,-1.0]])],"derivedFrom":subQ1}),1.0]])]});}
            var Q78;
            {var subQ5=sQuery(id+"F0.wireOp",EDGE,"E8.1");var subQ6=sQuery(id+"F0.wireOp",EDGE,"E7");var subQ7=makeQuery(id+"F0.imprint","INTERSECT",VERTEX,{"derivedFrom":[subQ6,subQ5]});Q78=makeQuery(id+"F0.imprint","IMPRINT",FACE,{"disambiguationData":[TD([[makeQuery(id+"F0.imprint","IMPRINT",EDGE,{"disambiguationData":[TD([[subQ7,-1.0]])],"derivedFrom":subQ6}),1.0]])]});}
            var Q79;
            {var subQ0=sQuery(id+"F0.wireOp",EDGE,"E17");var subQ1=sQuery(id+"F0.wireOp",EDGE,"E1.4");var subQ2=makeQuery(id+"F0.imprint","INTERSECT",VERTEX,{"derivedFrom":[subQ1,subQ0]});Q79=makeQuery(id+"F0.imprint","IMPRINT",FACE,{"disambiguationData":[TD([[makeQuery(id+"F0.imprint","IMPRINT",EDGE,{"disambiguationData":[TD([[subQ2,1.0]])],"derivedFrom":subQ1}),-1.0]])]});}
            var Q80;
            {var subQ0=sQuery(id+"F0.wireOp",EDGE,"E17");var subQ1=sQuery(id+"F0.wireOp",EDGE,"E1.3");var subQ2=makeQuery(id+"F0.imprint","INTERSECT",VERTEX,{"derivedFrom":[subQ1,subQ0]});Q80=makeQuery(id+"F0.imprint","IMPRINT",FACE,{"disambiguationData":[TD([[makeQuery(id+"F0.imprint","IMPRINT",EDGE,{"disambiguationData":[TD([[subQ2,-1.0]])],"derivedFrom":subQ1}),-1.0]])]});}
            var Q81;
            {var subQ0=sQuery(id+"F0.wireOp",EDGE,"E17");var subQ1=sQuery(id+"F0.wireOp",EDGE,"E6");var subQ2=makeQuery(id+"F0.imprint","INTERSECT",VERTEX,{"derivedFrom":[subQ1,subQ0]});Q81=makeQuery(id+"F0.imprint","IMPRINT",FACE,{"disambiguationData":[TD([[makeQuery(id+"F0.imprint","IMPRINT",EDGE,{"disambiguationData":[TD([[subQ2,-1.0]])],"derivedFrom":subQ1}),-1.0]])]});}
            var Q82;
            {var subQ0=sQuery(id+"F0.wireOp",EDGE,"E8.2");var subQ1=sQuery(id+"F0.wireOp",EDGE,"E6");var subQ2=makeQuery(id+"F0.imprint","INTERSECT",VERTEX,{"derivedFrom":[subQ1,subQ0]});Q82=makeQuery(id+"F0.imprint","IMPRINT",FACE,{"disambiguationData":[TD([[makeQuery(id+"F0.imprint","IMPRINT",EDGE,{"disambiguationData":[TD([[subQ2,-1.0]])],"derivedFrom":subQ1}),1.0]])]});}
            var Q83;
            {var subQ0=sQuery(id+"F0.wireOp",EDGE,"E25");var subQ1=sQuery(id+"F0.wireOp",EDGE,"E7");var subQ2=makeQuery(id+"F0.imprint","INTERSECT",VERTEX,{"derivedFrom":[subQ1,subQ0]});Q83=makeQuery(id+"F0.imprint","IMPRINT",FACE,{"disambiguationData":[TD([[makeQuery(id+"F0.imprint","IMPRINT",EDGE,{"disambiguationData":[TD([[subQ2,-1.0]])],"derivedFrom":subQ1}),1.0]])]});}
            var Q84;
            {var subQ0=sQuery(id+"F0.wireOp",EDGE,"E8.1");var subQ1=sQuery(id+"F0.wireOp",EDGE,"E7");var subQ2=makeQuery(id+"F0.imprint","INTERSECT",VERTEX,{"derivedFrom":[subQ1,subQ0]});Q84=makeQuery(id+"F0.imprint","IMPRINT",FACE,{"disambiguationData":[TD([[makeQuery(id+"F0.imprint","IMPRINT",EDGE,{"disambiguationData":[TD([[subQ2,-1.0]])],"derivedFrom":subQ1}),-1.0]])]});}
            var Q85;
            {var subQ3=sQuery(id+"F0.wireOp",EDGE,"E18");var subQ5=sQuery(id+"F0.wireOp",EDGE,"E1.2");var subQ6=makeQuery(id+"F0.imprint","INTERSECT",VERTEX,{"derivedFrom":[subQ5,subQ3]});Q85=makeQuery(id+"F0.imprint","IMPRINT",FACE,{"disambiguationData":[TD([[makeQuery(id+"F0.imprint","IMPRINT",EDGE,{"disambiguationData":[TD([[subQ6,-1.0]])],"derivedFrom":subQ5}),-1.0]])]});}
            var Q86;
            {var subQ0=sQuery(id+"F0.wireOp",EDGE,"E24");var subQ1=sQuery(id+"F0.wireOp",EDGE,"E9");var subQ2=makeQuery(id+"F0.imprint","INTERSECT",VERTEX,{"derivedFrom":[subQ1,subQ0]});Q86=makeQuery(id+"F0.imprint","IMPRINT",FACE,{"disambiguationData":[TD([[makeQuery(id+"F0.imprint","IMPRINT",EDGE,{"disambiguationData":[TD([[subQ2,-1.0]])],"derivedFrom":subQ1}),1.0]])]});}
            var Q87;
            {var subQ5=sQuery(id+"F0.wireOp",EDGE,"E2");var subQ7=sQuery(id+"F0.wireOp",EDGE,"E8.0");var subQ8=makeQuery(id+"F0.imprint","INTERSECT",VERTEX,{"derivedFrom":[subQ5,subQ7]});Q87=makeQuery(id+"F0.imprint","IMPRINT",FACE,{"disambiguationData":[TD([[makeQuery(id+"F0.imprint","IMPRINT",EDGE,{"disambiguationData":[TD([[subQ8,-1.0]])],"derivedFrom":subQ5}),1.0]])]});}
            var Q88;
            {var subQ0=sQuery(id+"F0.wireOp",EDGE,"E18");var subQ1=sQuery(id+"F0.wireOp",EDGE,"E1.3");var subQ2=makeQuery(id+"F0.imprint","INTERSECT",VERTEX,{"derivedFrom":[subQ1,subQ0]});Q88=makeQuery(id+"F0.imprint","IMPRINT",FACE,{"disambiguationData":[TD([[makeQuery(id+"F0.imprint","IMPRINT",EDGE,{"disambiguationData":[TD([[subQ2,1.0]])],"derivedFrom":subQ1}),-1.0]])]});}
            var Q89;
            {var subQ0=sQuery(id+"F0.wireOp",EDGE,"E18");var subQ6=sQuery(id+"F0.wireOp",EDGE,"E3");var subQ9=makeQuery(id+"F0.imprint","INTERSECT",VERTEX,{"derivedFrom":[subQ6,subQ0]});Q89=makeQuery(id+"F0.imprint","IMPRINT",FACE,{"disambiguationData":[TD([[makeQuery(id+"F0.imprint","IMPRINT",EDGE,{"disambiguationData":[TD([[subQ9,-1.0]])],"derivedFrom":subQ6}),1.0]])]});}
            var Q90;
            {var subQ0=sQuery(id+"F0.wireOp",EDGE,"E18");var subQ1=sQuery(id+"F0.wireOp",EDGE,"E3");var subQ2=makeQuery(id+"F0.imprint","INTERSECT",VERTEX,{"derivedFrom":[subQ1,subQ0]});Q90=makeQuery(id+"F0.imprint","IMPRINT",FACE,{"disambiguationData":[TD([[makeQuery(id+"F0.imprint","IMPRINT",EDGE,{"disambiguationData":[TD([[subQ2,-1.0]])],"derivedFrom":subQ1}),-1.0]])]});}
            var Q91;
            {var subQ0=sQuery(id+"F0.wireOp",EDGE,"E8.1");var subQ1=sQuery(id+"F0.wireOp",EDGE,"E3");var subQ2=makeQuery(id+"F0.imprint","INTERSECT",VERTEX,{"derivedFrom":[subQ1,subQ0]});Q91=makeQuery(id+"F0.imprint","IMPRINT",FACE,{"disambiguationData":[TD([[makeQuery(id+"F0.imprint","IMPRINT",EDGE,{"disambiguationData":[TD([[subQ2,-1.0]])],"derivedFrom":subQ1}),1.0]])]});}
            var Q92;
            {var subQ0=sQuery(id+"F0.wireOp",EDGE,"E8.0");var subQ1=sQuery(id+"F0.wireOp",EDGE,"E2");var subQ2=makeQuery(id+"F0.imprint","INTERSECT",VERTEX,{"derivedFrom":[subQ1,subQ0]});Q92=makeQuery(id+"F0.imprint","IMPRINT",FACE,{"disambiguationData":[TD([[makeQuery(id+"F0.imprint","IMPRINT",EDGE,{"disambiguationData":[TD([[subQ2,-1.0]])],"derivedFrom":subQ1}),-1.0]])]});}
            var Q93;
            {var subQ0=sQuery(id+"F0.wireOp",EDGE,"E24");var subQ1=sQuery(id+"F0.wireOp",EDGE,"E2");var subQ2=makeQuery(id+"F0.imprint","INTERSECT",VERTEX,{"derivedFrom":[subQ1,subQ0]});Q93=makeQuery(id+"F0.imprint","IMPRINT",FACE,{"disambiguationData":[TD([[makeQuery(id+"F0.imprint","IMPRINT",EDGE,{"disambiguationData":[TD([[subQ2,-1.0]])],"derivedFrom":subQ1}),1.0]])]});}
            var Q94;
            {var subQ0=sQuery(id+"F0.wireOp",EDGE,"E19");var subQ1=sQuery(id+"F0.wireOp",EDGE,"E1.1");var subQ2=makeQuery(id+"F0.imprint","INTERSECT",VERTEX,{"derivedFrom":[subQ1,subQ0]});Q94=makeQuery(id+"F0.imprint","IMPRINT",FACE,{"disambiguationData":[TD([[makeQuery(id+"F0.imprint","IMPRINT",EDGE,{"disambiguationData":[TD([[subQ2,-1.0]])],"derivedFrom":subQ1}),-1.0]])]});}
            var Q95;
            {var subQ0=sQuery(id+"F0.wireOp",EDGE,"E23");var subQ1=sQuery(id+"F0.wireOp",EDGE,"E11");var subQ2=makeQuery(id+"F0.imprint","INTERSECT",VERTEX,{"derivedFrom":[subQ1,subQ0]});Q95=makeQuery(id+"F0.imprint","IMPRINT",FACE,{"disambiguationData":[TD([[makeQuery(id+"F0.imprint","IMPRINT",EDGE,{"disambiguationData":[TD([[subQ2,-1.0]])],"derivedFrom":subQ1}),1.0]])]});}
            var Q96;
            {var subQ1=sQuery(id+"F0.wireOp",EDGE,"E4");var subQ7=sQuery(id+"F0.wireOp",EDGE,"E8.5");var subQ8=makeQuery(id+"F0.imprint","INTERSECT",VERTEX,{"derivedFrom":[subQ1,subQ7]});Q96=makeQuery(id+"F0.imprint","IMPRINT",FACE,{"disambiguationData":[TD([[makeQuery(id+"F0.imprint","IMPRINT",EDGE,{"disambiguationData":[TD([[subQ8,-1.0]])],"derivedFrom":subQ1}),1.0]])]});}
            var Q97;
            {var subQ0=sQuery(id+"F0.wireOp",EDGE,"E19");var subQ1=sQuery(id+"F0.wireOp",EDGE,"E5");var subQ2=makeQuery(id+"F0.imprint","INTERSECT",VERTEX,{"derivedFrom":[subQ1,subQ0]});Q97=makeQuery(id+"F0.imprint","IMPRINT",FACE,{"disambiguationData":[TD([[makeQuery(id+"F0.imprint","IMPRINT",EDGE,{"disambiguationData":[TD([[subQ2,-1.0]])],"derivedFrom":subQ1}),1.0]])]});}
            var Q98;
            {var subQ3=sQuery(id+"F0.wireOp",EDGE,"E19");var subQ5=sQuery(id+"F0.wireOp",EDGE,"E1.2");var subQ6=makeQuery(id+"F0.imprint","INTERSECT",VERTEX,{"derivedFrom":[subQ5,subQ3]});Q98=makeQuery(id+"F0.imprint","IMPRINT",FACE,{"disambiguationData":[TD([[makeQuery(id+"F0.imprint","IMPRINT",EDGE,{"disambiguationData":[TD([[subQ6,1.0]])],"derivedFrom":subQ5}),-1.0]])]});}
            var Q99;
            {var subQ0=sQuery(id+"F0.wireOp",EDGE,"E8.0");var subQ1=sQuery(id+"F0.wireOp",EDGE,"E5");var subQ2=makeQuery(id+"F0.imprint","INTERSECT",VERTEX,{"derivedFrom":[subQ1,subQ0]});Q99=makeQuery(id+"F0.imprint","IMPRINT",FACE,{"disambiguationData":[TD([[makeQuery(id+"F0.imprint","IMPRINT",EDGE,{"disambiguationData":[TD([[subQ2,-1.0]])],"derivedFrom":subQ1}),1.0]])]});}
            var Q100;
            {var subQ0=sQuery(id+"F0.wireOp",EDGE,"E23");var subQ1=sQuery(id+"F0.wireOp",EDGE,"E4");var subQ2=makeQuery(id+"F0.imprint","INTERSECT",VERTEX,{"derivedFrom":[subQ1,subQ0]});Q100=makeQuery(id+"F0.imprint","IMPRINT",FACE,{"disambiguationData":[TD([[makeQuery(id+"F0.imprint","IMPRINT",EDGE,{"disambiguationData":[TD([[subQ2,-1.0]])],"derivedFrom":subQ1}),1.0]])]});}
            var Q101;
            {var subQ0=sQuery(id+"F0.wireOp",EDGE,"E8.5");var subQ1=sQuery(id+"F0.wireOp",EDGE,"E4");var subQ2=makeQuery(id+"F0.imprint","INTERSECT",VERTEX,{"derivedFrom":[subQ1,subQ0]});Q101=makeQuery(id+"F0.imprint","IMPRINT",FACE,{"disambiguationData":[TD([[makeQuery(id+"F0.imprint","IMPRINT",EDGE,{"disambiguationData":[TD([[subQ2,-1.0]])],"derivedFrom":subQ1}),-1.0]])]});}
            var Q102;
            {var subQ0=sQuery(id+"F0.wireOp",EDGE,"E19");var subQ1=sQuery(id+"F0.wireOp",EDGE,"E5");var subQ2=makeQuery(id+"F0.imprint","INTERSECT",VERTEX,{"derivedFrom":[subQ1,subQ0]});Q102=makeQuery(id+"F0.imprint","IMPRINT",FACE,{"disambiguationData":[TD([[makeQuery(id+"F0.imprint","IMPRINT",EDGE,{"disambiguationData":[TD([[subQ2,-1.0]])],"derivedFrom":subQ1}),-1.0]])]});}
            extrude(context, id + "F1", {"entities" : qUnion([Q0, Q1, Q2, Q3, Q4, Q5, Q6, Q7, Q8, Q9, Q10, Q11, Q12, Q13, Q14, Q15, Q16, Q17, Q18, Q19, Q20, Q21, Q22, Q23, Q24, Q25, Q26, Q27, Q28, Q29, Q30, Q31, Q32, Q33, Q34, Q35, Q36, Q37, Q38, Q39, Q40, Q41, Q42, Q43, Q44, Q45, Q46, Q47, Q48, Q49, Q50, Q51, Q52, Q53, Q54, Q55, Q56, Q57, Q58, Q59, Q60, Q61, Q62, Q63, Q64, Q65, Q66, Q67, Q68, Q69, Q70, Q71, Q72, Q73, Q74, Q75, Q76, Q77, Q78, Q79, Q80, Q81, Q82, Q83, Q84, Q85, Q86, Q87, Q88, Q89, Q90, Q91, Q92, Q93, Q94, Q95, Q96, Q97, Q98, Q99, Q100, Q101, Q102]), "depth" : 7 * mm, "offsetDistance" : 25 * mm});
        }
    });
